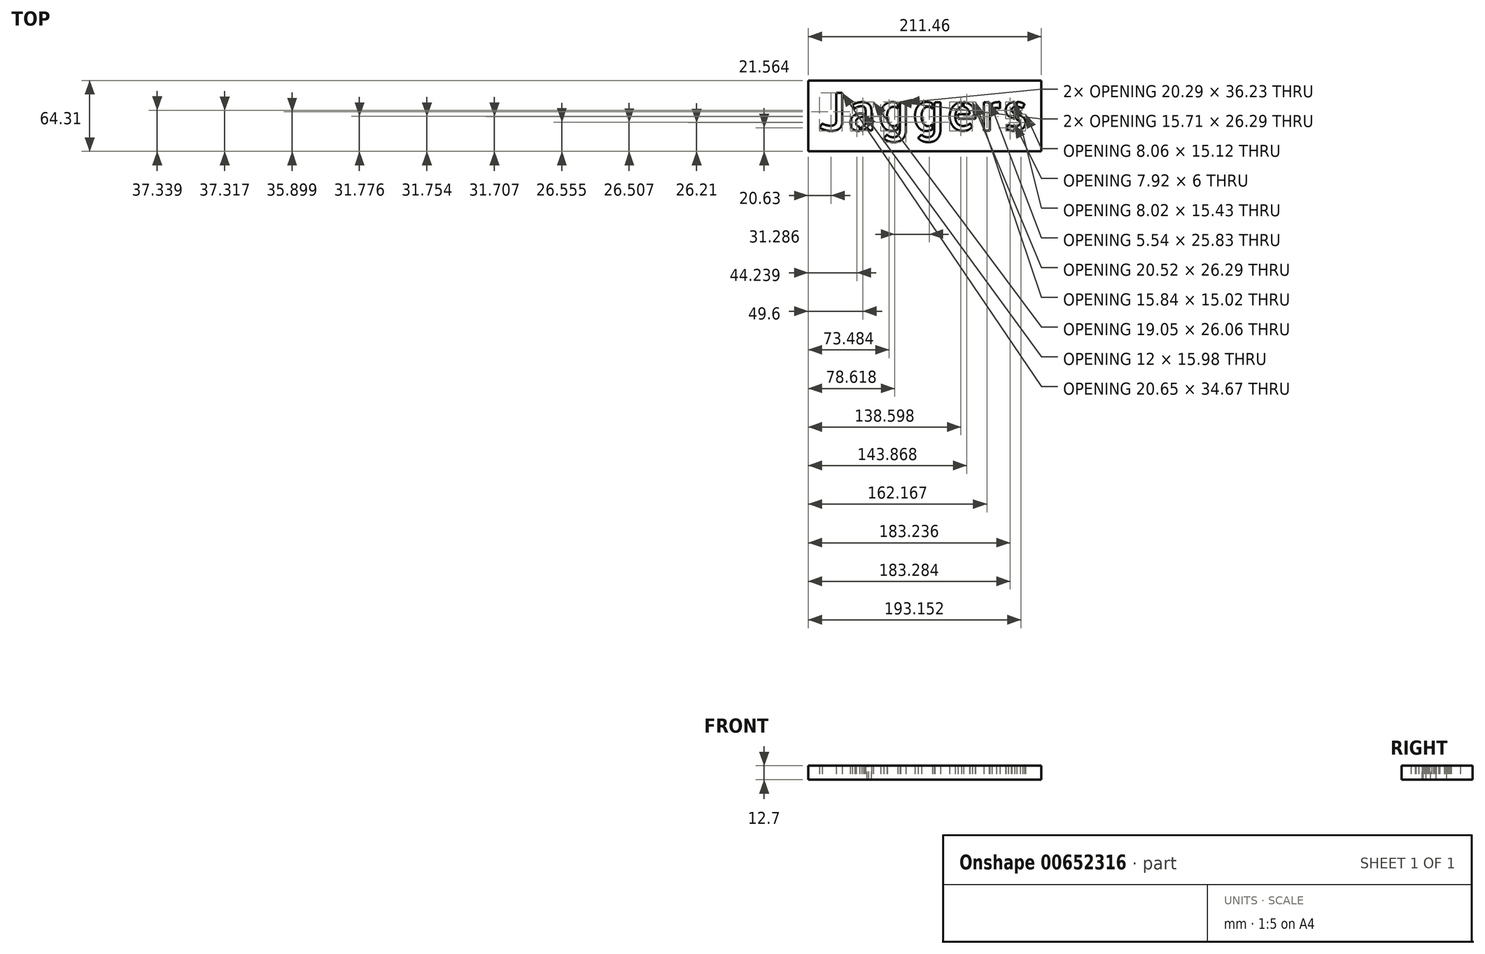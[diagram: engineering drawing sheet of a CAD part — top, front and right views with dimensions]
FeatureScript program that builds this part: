
annotation { "Feature Type Name" : "Feature", "Feature Type Description" : "" }
export const myFeature = defineFeature(function(context is Context, id is Id, definition is map)
    precondition{}
    {
        {
            var Q0;
            Q0=qCreatedBy(makeId("Top.planeOp"),FACE);
            var sketch = newSketch(context, id + "F0", { "sketchPlane" : qUnion([Q0])});
            skText(sketch, "E0", { "text": "Jaggers", "fontName": "AllertaStencil-Regular.ttf"});
            skLineSegment(sketch, "E1.bottom", {"start": v(-116.16, 27.75) * mm, "end": v(95.3, 27.75) * mm});
            skLineSegment(sketch, "E1.top", {"start": v(-116.16, -36.56) * mm, "end": v(95.3, -36.56) * mm});
            skLineSegment(sketch, "E1.left", {"start": v(-116.16, 27.75) * mm, "end": v(-116.16, -36.56) * mm});
            skLineSegment(sketch, "E1.right", {"start": v(95.3, 27.75) * mm, "end": v(95.3, -36.56) * mm});
            const initialGuessF0  = {"E0": [-0.10705, -0.01777, 1, 0, 0.03377]};
            skSetInitialGuess(sketch, initialGuessF0);
            skSolve(sketch);
        }
        {
            var Q0;
            Q0=makeQuery(id+"F0.imprint","IMPRINT",FACE,{"disambiguationData":[TD([[makeQuery(id+"F0.imprint","IMPRINT",EDGE,{"derivedFrom":sQuery(id+"F0.wireOp",EDGE,"E0.sketch_text.stroke-0")}),1.0]])]});
            extrude(context, id + "F1", {"entities" : qUnion([Q0]), "depth" : 12.7 * mm, "offsetDistance" : 25.4 * mm});
        }
    });
